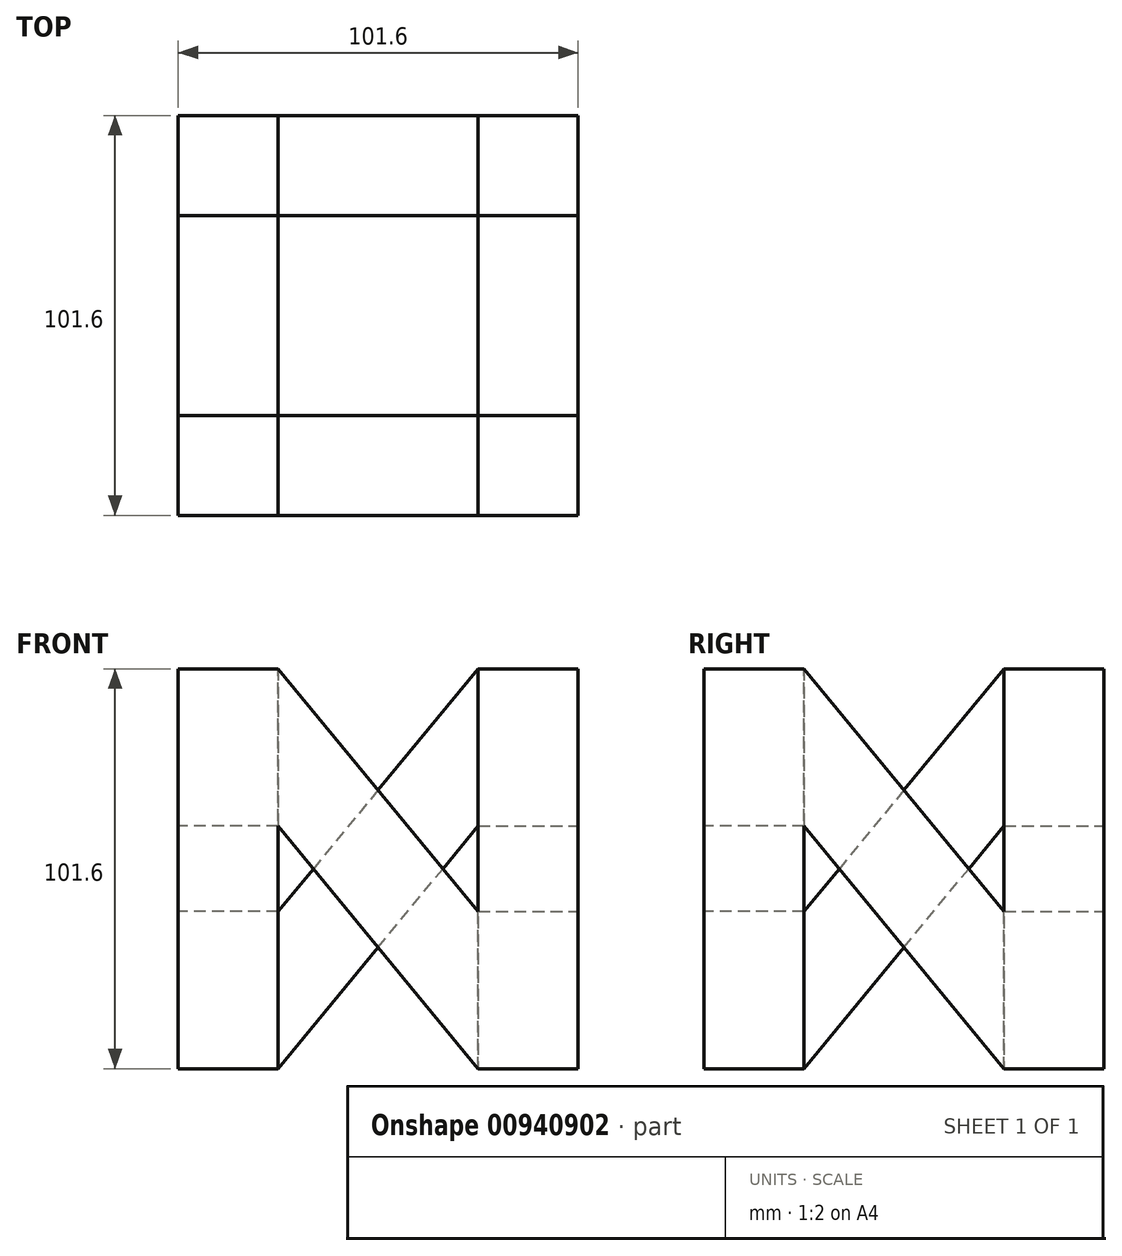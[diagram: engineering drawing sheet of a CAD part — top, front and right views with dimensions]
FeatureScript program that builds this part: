
annotation { "Feature Type Name" : "Feature", "Feature Type Description" : "" }
export const myFeature = defineFeature(function(context is Context, id is Id, definition is map)
    precondition{}
    {
        {
            var Q0;
            Q0=qCreatedBy(makeId("Front.planeOp"),FACE);
            var sketch = newSketch(context, id + "F0", { "sketchPlane" : qUnion([Q0])});
            skLineSegment(sketch, "E0.bottom", {"start": v(-50.8, 50.8) * mm, "end": v(50.8, 50.8) * mm});
            skLineSegment(sketch, "E0.top", {"start": v(-50.8, -50.8) * mm, "end": v(50.8, -50.8) * mm});
            skLineSegment(sketch, "E0.left", {"start": v(-50.8, 50.8) * mm, "end": v(-50.8, -50.8) * mm});
            skLineSegment(sketch, "E0.right", {"start": v(50.8, 50.8) * mm, "end": v(50.8, -50.8) * mm});
            skPoint(sketch, "E0.middle", {"position": v(0, 0) * mm});
            skSolve(sketch);
        }
        {
            var Q0;
            Q0=makeQuery(id+"F0.imprint","IMPRINT",FACE,{"disambiguationData":[TD([[makeQuery(id+"F0.imprint","IMPRINT",EDGE,{"derivedFrom":sQuery(id+"F0.wireOp",EDGE,"E0.bottom")}),-1.0]])]});
            extrude(context, id + "F1", {"entities" : qUnion([Q0]), "depth" : 25.4 * mm, "offsetDistance" : 25.4 * mm});
        }
        {
            var Q0;
            Q0=makeQuery(id+"F1.opExtrude","CAP_FACE",FACE,{"disambiguationData":[OSD([sQuery(id+"F0.wireOp",EDGE,"E0.bottom"),sQuery(id+"F0.wireOp",EDGE,"E0.top"),sQuery(id+"F0.wireOp",EDGE,"E0.left"),sQuery(id+"F0.wireOp",EDGE,"E0.right")])],"isStart":false});
            var sketch = newSketch(context, id + "F2", { "sketchPlane" : qUnion([Q0])});
            skLineSegment(sketch, "E1", {"start": v(-50.8, 50.8) * mm, "end": v(-25.4, 50.8) * mm});
            skLineSegment(sketch, "E2", {"start": v(-25.4, 50.8) * mm, "end": v(25.4, -10.86) * mm});
            skLineSegment(sketch, "E3", {"start": v(25.4, -10.86) * mm, "end": v(25.4, 50.8) * mm});
            skLineSegment(sketch, "E4", {"start": v(25.4, 50.8) * mm, "end": v(50.8, 50.8) * mm});
            skLineSegment(sketch, "E5", {"start": v(50.8, 50.8) * mm, "end": v(50.8, -50.8) * mm});
            skLineSegment(sketch, "E6", {"start": v(50.8, -50.8) * mm, "end": v(25.4, -50.8) * mm});
            skLineSegment(sketch, "E7", {"start": v(25.4, -50.8) * mm, "end": v(-25.4, 10.86) * mm});
            skLineSegment(sketch, "E8", {"start": v(-25.4, 10.86) * mm, "end": v(-25.4, -50.8) * mm});
            skLineSegment(sketch, "E9", {"start": v(-25.4, -50.8) * mm, "end": v(-50.8, -50.8) * mm});
            skLineSegment(sketch, "E10", {"start": v(-50.8, -50.8) * mm, "end": v(-50.8, 50.8) * mm});
            skSolve(sketch);
        }
        {
            var Q0;
            {var subQ0=sQuery(id+"F2.wireOp",EDGE,"E2");Q0=makeQuery(id+"F2.imprint","IMPRINT",FACE,{"disambiguationData":[TD([[makeQuery(id+"F2.imprint","IMPRINT",EDGE,{"derivedFrom":subQ0}),1.0]])]});}
            var Q1;
            {var subQ0=sQuery(id+"F2.wireOp",EDGE,"E7");Q1=makeQuery(id+"F2.imprint","IMPRINT",FACE,{"disambiguationData":[TD([[makeQuery(id+"F2.imprint","IMPRINT",EDGE,{"derivedFrom":subQ0}),1.0]])]});}
            extrude(context, id + "F3", {"entities" : qUnion([Q0, Q1]), "operationType" : NewBodyOperationType.REMOVE, "endBound" : BoundingType.THROUGH_ALL, "oppositeDirection" : true, "depth" : 25.4 * mm, "offsetDistance" : 25.4 * mm});
        }
        {
            var Q0;
            Q0=makeQuery(id+"F1.opExtrude","CAP_FACE",FACE,{"disambiguationData":[OSD([sQuery(id+"F0.wireOp",EDGE,"E0.bottom"),sQuery(id+"F0.wireOp",EDGE,"E0.top"),sQuery(id+"F0.wireOp",EDGE,"E0.left"),sQuery(id+"F0.wireOp",EDGE,"E0.right")])],"isStart":true});
            var sketch = newSketch(context, id + "F4", { "sketchPlane" : qUnion([Q0])});
            skLineSegment(sketch, "E11.bottom", {"start": v(-50.8, 50.8) * mm, "end": v(-25.4, 50.8) * mm});
            skLineSegment(sketch, "E11.top", {"start": v(-50.8, -50.8) * mm, "end": v(-25.4, -50.8) * mm});
            skLineSegment(sketch, "E11.left", {"start": v(-50.8, 50.8) * mm, "end": v(-50.8, -50.8) * mm});
            skLineSegment(sketch, "E11.right", {"start": v(-25.4, 50.8) * mm, "end": v(-25.4, -50.8) * mm});
            skSolve(sketch);
        }
        {
            var Q0;
            {var subQ3=sQuery(id+"F4.wireOp",EDGE,"E11.bottom");Q0=makeQuery(id+"F4.imprint","IMPRINT",FACE,{"disambiguationData":[TD([[makeQuery(id+"F4.imprint","IMPRINT",EDGE,{"derivedFrom":subQ3}),1.0]])]});}
            extrude(context, id + "F5", {"entities" : qUnion([Q0]), "operationType" : NewBodyOperationType.ADD, "depth" : 76.2 * mm, "offsetDistance" : 25.4 * mm});
        }
        {
            var Q0;
            Q0=makeQuery(id+"F5.boolean.opBoolean","MERGE",FACE,{"derivedFrom":[makeQuery(id+"F1.opExtrude","SWEPT_FACE",FACE,{"disambiguationData":[OSD([sQuery(id+"F0.wireOp",EDGE,"E0.right")])]}),makeQuery(id+"F5.opExtrude","SWEPT_FACE",FACE,{"disambiguationData":[OSD([sQuery(id+"F4.wireOp",EDGE,"E11.left")])]})]});
            var sketch = newSketch(context, id + "F6", { "sketchPlane" : qUnion([Q0])});
            skLineSegment(sketch, "E12", {"start": v(-25.4, 50.8) * mm, "end": v(0, 50.8) * mm});
            skLineSegment(sketch, "E13", {"start": v(0, 50.8) * mm, "end": v(50.8, -10.86) * mm});
            skLineSegment(sketch, "E14", {"start": v(50.8, -10.86) * mm, "end": v(50.8, 50.8) * mm});
            skLineSegment(sketch, "E15", {"start": v(50.8, 50.8) * mm, "end": v(76.2, 50.8) * mm});
            skLineSegment(sketch, "E16", {"start": v(76.2, 50.8) * mm, "end": v(76.2, -50.8) * mm});
            skLineSegment(sketch, "E17", {"start": v(76.2, -50.8) * mm, "end": v(50.8, -50.8) * mm});
            skLineSegment(sketch, "E18", {"start": v(50.8, -50.8) * mm, "end": v(0, 10.86) * mm});
            skLineSegment(sketch, "E19", {"start": v(0, 10.86) * mm, "end": v(0, -50.8) * mm});
            skLineSegment(sketch, "E20", {"start": v(0, -50.8) * mm, "end": v(-25.4, -50.8) * mm});
            skLineSegment(sketch, "E21", {"start": v(-25.4, -50.8) * mm, "end": v(-25.4, 50.8) * mm});
            skSolve(sketch);
        }
        {
            var Q0;
            {var subQ0=sQuery(id+"F6.wireOp",EDGE,"E13");Q0=makeQuery(id+"F6.imprint","IMPRINT",FACE,{"disambiguationData":[TD([[makeQuery(id+"F6.imprint","IMPRINT",EDGE,{"derivedFrom":subQ0}),1.0]])]});}
            var Q1;
            {var subQ0=sQuery(id+"F6.wireOp",EDGE,"E18");Q1=makeQuery(id+"F6.imprint","IMPRINT",FACE,{"disambiguationData":[TD([[makeQuery(id+"F6.imprint","IMPRINT",EDGE,{"derivedFrom":subQ0}),1.0]])]});}
            extrude(context, id + "F7", {"entities" : qUnion([Q0, Q1]), "operationType" : NewBodyOperationType.REMOVE, "oppositeDirection" : true, "depth" : 25.4 * mm, "offsetDistance" : 25.4 * mm});
        }
        {
            var Q0;
            Q0=makeQuery(id+"F5.boolean.opBoolean","MERGE",FACE,{"derivedFrom":[makeQuery(id+"F3.boolean.opBoolean","COPY",FACE,{"derivedFrom":makeQuery(id+"F3.opExtrude","SWEPT_FACE",FACE,{"disambiguationData":[OSD([sQuery(id+"F2.wireOp",EDGE,"E3")])]})}),makeQuery(id+"F5.opExtrude","SWEPT_FACE",FACE,{"disambiguationData":[OSD([sQuery(id+"F4.wireOp",EDGE,"E11.right")])]})]});
            var sketch = newSketch(context, id + "F8", { "sketchPlane" : qUnion([Q0])});
            skLineSegment(sketch, "E22.bottom", {"start": v(-50.8, 50.8) * mm, "end": v(-76.2, 50.8) * mm});
            skLineSegment(sketch, "E22.top", {"start": v(-50.8, -50.8) * mm, "end": v(-76.2, -50.8) * mm});
            skLineSegment(sketch, "E22.left", {"start": v(-50.8, 50.8) * mm, "end": v(-50.8, -50.8) * mm});
            skLineSegment(sketch, "E22.right", {"start": v(-76.2, 50.8) * mm, "end": v(-76.2, -50.8) * mm});
            skSolve(sketch);
        }
        {
            var Q0;
            {var subQ3=sQuery(id+"F8.wireOp",EDGE,"E22.bottom");Q0=makeQuery(id+"F8.imprint","IMPRINT",FACE,{"disambiguationData":[TD([[makeQuery(id+"F8.imprint","IMPRINT",EDGE,{"derivedFrom":subQ3}),-1.0]])]});}
            extrude(context, id + "F9", {"entities" : qUnion([Q0]), "operationType" : NewBodyOperationType.ADD, "depth" : 76.2 * mm, "offsetDistance" : 25.4 * mm});
        }
        {
            var Q0;
            Q0=makeQuery(id+"F9.boolean.opBoolean","MERGE",FACE,{"derivedFrom":[makeQuery(id+"F5.opExtrude","CAP_FACE",FACE,{"disambiguationData":[OSD([sQuery(id+"F4.wireOp",EDGE,"E11.bottom"),sQuery(id+"F4.wireOp",EDGE,"E11.top"),sQuery(id+"F4.wireOp",EDGE,"E11.left"),sQuery(id+"F4.wireOp",EDGE,"E11.right")])],"isStart":false}),makeQuery(id+"F9.opExtrude","SWEPT_FACE",FACE,{"disambiguationData":[OSD([sQuery(id+"F8.wireOp",EDGE,"E22.right")])]})]});
            var sketch = newSketch(context, id + "F10", { "sketchPlane" : qUnion([Q0])});
            skLineSegment(sketch, "E23", {"start": v(-50.8, 50.8) * mm, "end": v(-25.4, 50.8) * mm});
            skLineSegment(sketch, "E24", {"start": v(-25.4, 50.8) * mm, "end": v(25.4, -10.86) * mm});
            skLineSegment(sketch, "E25", {"start": v(25.4, -10.86) * mm, "end": v(25.4, 50.8) * mm});
            skLineSegment(sketch, "E26", {"start": v(25.4, 50.8) * mm, "end": v(50.8, 50.8) * mm});
            skLineSegment(sketch, "E27", {"start": v(50.8, 50.8) * mm, "end": v(50.8, -50.8) * mm});
            skLineSegment(sketch, "E28", {"start": v(50.8, -50.8) * mm, "end": v(25.4, -50.8) * mm});
            skLineSegment(sketch, "E29", {"start": v(25.4, -50.8) * mm, "end": v(-25.4, 10.86) * mm});
            skLineSegment(sketch, "E30", {"start": v(-25.4, 10.86) * mm, "end": v(-25.4, -50.8) * mm});
            skLineSegment(sketch, "E31", {"start": v(-25.4, -50.8) * mm, "end": v(-50.8, -50.8) * mm});
            skLineSegment(sketch, "E32", {"start": v(-50.8, -50.8) * mm, "end": v(-50.8, 50.8) * mm});
            skSolve(sketch);
        }
        {
            var Q0;
            {var subQ0=sQuery(id+"F10.wireOp",EDGE,"E24");Q0=makeQuery(id+"F10.imprint","IMPRINT",FACE,{"disambiguationData":[TD([[makeQuery(id+"F10.imprint","IMPRINT",EDGE,{"derivedFrom":subQ0}),1.0]])]});}
            var Q1;
            {var subQ0=sQuery(id+"F10.wireOp",EDGE,"E29");Q1=makeQuery(id+"F10.imprint","IMPRINT",FACE,{"disambiguationData":[TD([[makeQuery(id+"F10.imprint","IMPRINT",EDGE,{"derivedFrom":subQ0}),1.0]])]});}
            extrude(context, id + "F11", {"entities" : qUnion([Q0, Q1]), "operationType" : NewBodyOperationType.REMOVE, "oppositeDirection" : true, "depth" : 25.4 * mm, "offsetDistance" : 25.4 * mm});
        }
        {
            var Q0;
            Q0=makeQuery(id+"F9.boolean.opBoolean","MERGE",FACE,{"derivedFrom":[makeQuery(id+"F7.boolean.opBoolean","COPY",FACE,{"derivedFrom":makeQuery(id+"F7.opExtrude","SWEPT_FACE",FACE,{"disambiguationData":[OSD([sQuery(id+"F6.wireOp",EDGE,"E14")])]})}),makeQuery(id+"F9.opExtrude","SWEPT_FACE",FACE,{"disambiguationData":[OSD([sQuery(id+"F8.wireOp",EDGE,"E22.left")])]})]});
            var sketch = newSketch(context, id + "F12", { "sketchPlane" : qUnion([Q0])});
            skLineSegment(sketch, "E33.bottom", {"start": v(-25.4, 50.8) * mm, "end": v(-50.8, 50.8) * mm});
            skLineSegment(sketch, "E33.top", {"start": v(-25.4, -50.8) * mm, "end": v(-50.8, -50.8) * mm});
            skLineSegment(sketch, "E33.left", {"start": v(-25.4, 50.8) * mm, "end": v(-25.4, -50.8) * mm});
            skLineSegment(sketch, "E33.right", {"start": v(-50.8, 50.8) * mm, "end": v(-50.8, -50.8) * mm});
            skSolve(sketch);
        }
        {
            var Q0;
            {var subQ3=sQuery(id+"F12.wireOp",EDGE,"E33.bottom");Q0=makeQuery(id+"F12.imprint","IMPRINT",FACE,{"disambiguationData":[TD([[makeQuery(id+"F12.imprint","IMPRINT",EDGE,{"derivedFrom":subQ3}),-1.0]])]});}
            extrude(context, id + "F13", {"entities" : qUnion([Q0]), "operationType" : NewBodyOperationType.ADD, "depth" : 50.8 * mm, "offsetDistance" : 25.4 * mm});
        }
        {
            var Q0;
            Q0=makeQuery(id+"F13.boolean.opBoolean","MERGE",FACE,{"derivedFrom":[makeQuery(id+"F1.opExtrude","SWEPT_FACE",FACE,{"disambiguationData":[OSD([sQuery(id+"F0.wireOp",EDGE,"E0.left")])]}),makeQuery(id+"F9.opExtrude","CAP_FACE",FACE,{"disambiguationData":[OSD([sQuery(id+"F8.wireOp",EDGE,"E22.bottom"),sQuery(id+"F8.wireOp",EDGE,"E22.top"),sQuery(id+"F8.wireOp",EDGE,"E22.left"),sQuery(id+"F8.wireOp",EDGE,"E22.right")])],"isStart":false}),makeQuery(id+"F13.opExtrude","SWEPT_FACE",FACE,{"disambiguationData":[OSD([sQuery(id+"F12.wireOp",EDGE,"E33.right")])]})]});
            var sketch = newSketch(context, id + "F14", { "sketchPlane" : qUnion([Q0])});
            skLineSegment(sketch, "E34", {"start": v(-76.2, 50.8) * mm, "end": v(-50.8, 50.8) * mm});
            skLineSegment(sketch, "E35", {"start": v(-50.8, 50.8) * mm, "end": v(0, -10.86) * mm});
            skLineSegment(sketch, "E36", {"start": v(0, -10.86) * mm, "end": v(0, 50.8) * mm});
            skLineSegment(sketch, "E37", {"start": v(0, 50.8) * mm, "end": v(25.4, 50.8) * mm});
            skLineSegment(sketch, "E38", {"start": v(25.4, 50.8) * mm, "end": v(25.4, -50.8) * mm});
            skLineSegment(sketch, "E39", {"start": v(25.4, -50.8) * mm, "end": v(0, -50.8) * mm});
            skLineSegment(sketch, "E40", {"start": v(0, -50.8) * mm, "end": v(-50.8, 10.86) * mm});
            skLineSegment(sketch, "E41", {"start": v(-50.8, 10.86) * mm, "end": v(-50.8, -50.8) * mm});
            skLineSegment(sketch, "E42", {"start": v(-50.8, -50.8) * mm, "end": v(-76.2, -50.8) * mm});
            skLineSegment(sketch, "E43", {"start": v(-76.2, -50.8) * mm, "end": v(-76.2, 50.8) * mm});
            skSolve(sketch);
        }
        {
            var Q0;
            {var subQ0=sQuery(id+"F14.wireOp",EDGE,"E35");Q0=makeQuery(id+"F14.imprint","IMPRINT",FACE,{"disambiguationData":[TD([[makeQuery(id+"F14.imprint","IMPRINT",EDGE,{"derivedFrom":subQ0}),1.0]])]});}
            var Q1;
            {var subQ0=sQuery(id+"F14.wireOp",EDGE,"E40");Q1=makeQuery(id+"F14.imprint","IMPRINT",FACE,{"disambiguationData":[TD([[makeQuery(id+"F14.imprint","IMPRINT",EDGE,{"derivedFrom":subQ0}),1.0]])]});}
            extrude(context, id + "F15", {"entities" : qUnion([Q0, Q1]), "operationType" : NewBodyOperationType.REMOVE, "oppositeDirection" : true, "depth" : 25.4 * mm, "offsetDistance" : 25.4 * mm});
        }
    });
